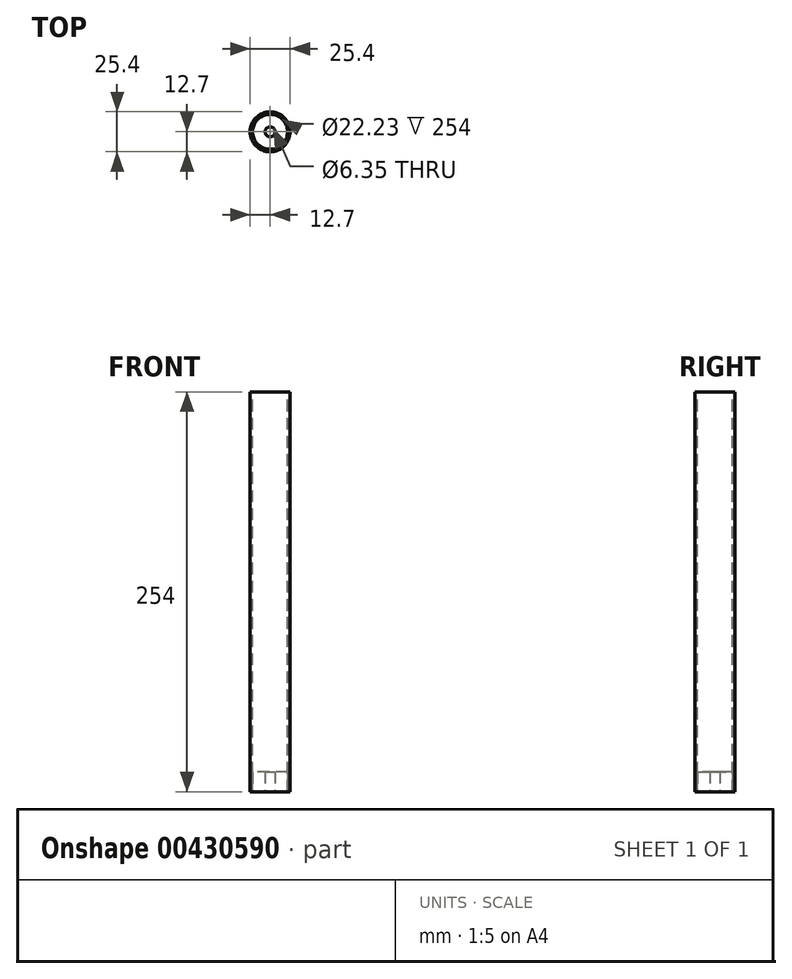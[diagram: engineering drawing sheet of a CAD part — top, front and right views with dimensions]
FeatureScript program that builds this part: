
annotation { "Feature Type Name" : "Feature", "Feature Type Description" : "" }
export const myFeature = defineFeature(function(context is Context, id is Id, definition is map)
    precondition{}
    {
        {
            var Q0;
            Q0=qCreatedBy(makeId("Top.planeOp"),FACE);
            var sketch = newSketch(context, id + "F0", { "sketchPlane" : qUnion([Q0])});
            skCircle(sketch, "E0", {"center": v(0, 0) * mm, "radius": 12.7 * mm});
            skSolve(sketch);
        }
        {
            var Q0;
            Q0=makeQuery(id+"F0.imprint","IMPRINT",FACE,{"disambiguationData":[TD([[makeQuery(id+"F0.imprint","IMPRINT",EDGE,{"derivedFrom":sQuery(id+"F0.wireOp",EDGE,"E0")}),1.0]])]});
            var sketch = newSketch(context, id + "F1", { "sketchPlane" : qUnion([Q0])});
            skCircle(sketch, "E1", {"center": v(0, 0) * mm, "radius": 11.11 * mm});
            skSolve(sketch);
        }
        {
            var Q0;
            Q0 = qSketchRegion(id + "F0", true);
            extrude(context, id + "F2", {"entities" : qUnion([Q0]), "endBound" : BoundingType.SYMMETRIC, "depth" : 254 * mm});
        }
        {
            var Q0;
            Q0 = qSketchRegion(id + "F1", true);
            extrude(context, id + "F3", {"entities" : qUnion([Q0]), "operationType" : NewBodyOperationType.REMOVE, "endBound" : BoundingType.SYMMETRIC, "oppositeDirection" : true, "depth" : 609.6 * mm});
        }
        {
            var Q0;
            Q0=makeQuery(id+"F2.opExtrude","CAP_FACE",FACE,{"disambiguationData":[OSD([sQuery(id+"F0.wireOp",EDGE,"E0")])],"isStart":true});
            var sketch = newSketch(context, id + "F4", { "sketchPlane" : qUnion([Q0])});
            skCircle(sketch, "E2", {"center": v(0, 0) * mm, "radius": 11.11 * mm});
            skSolve(sketch);
        }
        {
            var Q0;
            Q0=makeQuery(id+"F4.imprint","IMPRINT",FACE,{"disambiguationData":[TD([[makeQuery(id+"F4.imprint","IMPRINT",EDGE,{"derivedFrom":sQuery(id+"F4.wireOp",EDGE,"E2")}),-1.0]])]});
            extrude(context, id + "F5", {"entities" : qUnion([Q0]), "oppositeDirection" : true, "depth" : 12.7 * mm});
        }
        {
            var Q0;
            Q0=makeQuery(id+"F5.opExtrude","CAP_FACE",FACE,{"disambiguationData":[OSD([sQuery(id+"F4.wireOp",EDGE,"E2")])],"isStart":true});
            var sketch = newSketch(context, id + "F6", { "sketchPlane" : qUnion([Q0])});
            skCircle(sketch, "E3", {"center": v(0, 0) * mm, "radius": 3.18 * mm});
            skSolve(sketch);
        }
        {
            var Q0;
            Q0=makeQuery(id+"F6.imprint","IMPRINT",FACE,{"disambiguationData":[TD([[makeQuery(id+"F6.imprint","IMPRINT",EDGE,{"derivedFrom":sQuery(id+"F6.wireOp",EDGE,"E3")}),1.0]])]});
            extrude(context, id + "F7", {"entities" : qUnion([Q0]), "operationType" : NewBodyOperationType.REMOVE, "endBound" : BoundingType.THROUGH_ALL, "oppositeDirection" : true, "depth" : 25.4 * mm});
        }
    });
